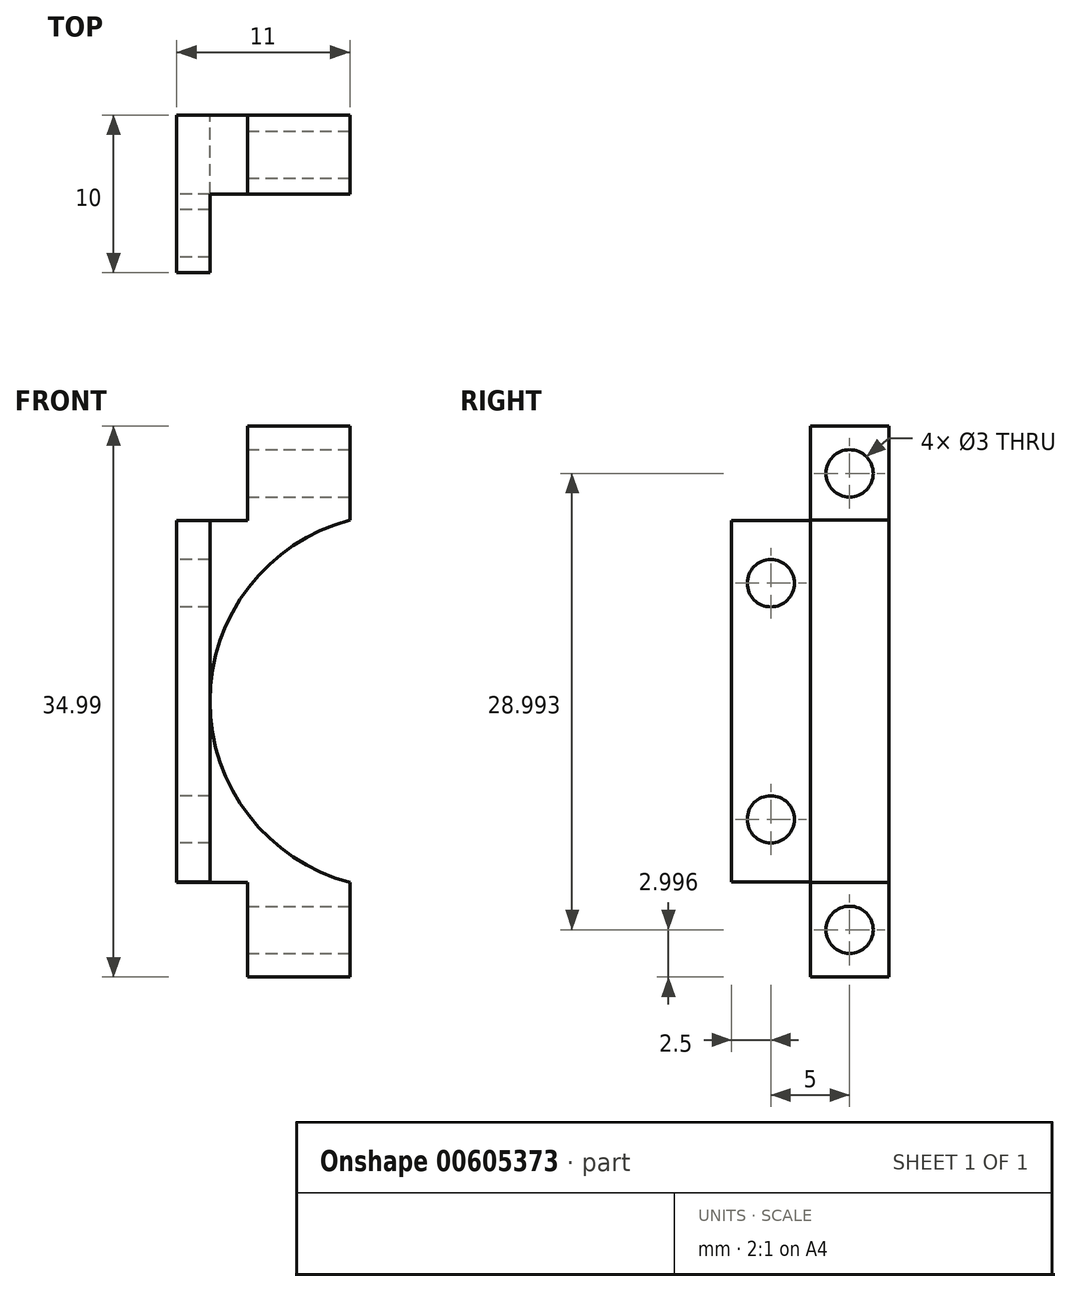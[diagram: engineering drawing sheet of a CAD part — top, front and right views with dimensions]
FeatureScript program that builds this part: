
annotation { "Feature Type Name" : "Feature", "Feature Type Description" : "" }
export const myFeature = defineFeature(function(context is Context, id is Id, definition is map)
    precondition{}
    {
        {
            var Q0;
            Q0=qCreatedBy(makeId("Front.planeOp"),FACE);
            var sketch = newSketch(context, id + "F0", { "sketchPlane" : qUnion([Q0])});
            skArc(sketch, "E0", {"start": v(0, 11.5) * mm, "mid": v(-8.88, 0) * mm, "end": v(0, -11.5) * mm});
            skLineSegment(sketch, "E1", {"start": v(0, -11.5) * mm, "end": v(0, -17.51) * mm});
            skLineSegment(sketch, "E2", {"start": v(0, -17.51) * mm, "end": v(-2, -17.51) * mm});
            skLineSegment(sketch, "E3", {"start": v(-2, -17.51) * mm, "end": v(-2, -11.51) * mm});
            skLineSegment(sketch, "E4", {"start": v(-2, -11.51) * mm, "end": v(-11, -11.51) * mm});
            skLineSegment(sketch, "E5", {"start": v(-11, -11.51) * mm, "end": v(-11, 11.48) * mm});
            skLineSegment(sketch, "E6", {"start": v(-11, 11.48) * mm, "end": v(-2, 11.48) * mm});
            skLineSegment(sketch, "E7", {"start": v(-2, 11.48) * mm, "end": v(-2, 17.48) * mm});
            skLineSegment(sketch, "E8", {"start": v(-2, 17.48) * mm, "end": v(0, 17.48) * mm});
            skLineSegment(sketch, "E9", {"start": v(0, 17.48) * mm, "end": v(0, 11.5) * mm});
            skLineSegment(sketch, "E10.bottom", {"start": v(-2, 17.48) * mm, "end": v(-6.5, 17.48) * mm});
            skLineSegment(sketch, "E10.top", {"start": v(-2, 11.48) * mm, "end": v(-6.5, 11.48) * mm});
            skLineSegment(sketch, "E10.left", {"start": v(-2, 17.48) * mm, "end": v(-2, 11.48) * mm});
            skLineSegment(sketch, "E10.right", {"start": v(-6.5, 17.48) * mm, "end": v(-6.5, 11.48) * mm});
            skLineSegment(sketch, "E11.bottom", {"start": v(-6.5, -11.51) * mm, "end": v(-2, -11.51) * mm});
            skLineSegment(sketch, "E11.top", {"start": v(-6.5, -17.51) * mm, "end": v(-2, -17.51) * mm});
            skLineSegment(sketch, "E11.left", {"start": v(-6.5, -11.51) * mm, "end": v(-6.5, -17.51) * mm});
            skLineSegment(sketch, "E11.right", {"start": v(-2, -11.51) * mm, "end": v(-2, -17.51) * mm});
            skSolve(sketch);
        }
        {
            var Q0;
            Q0=qSketchRegion(id+"F0",true);
            extrude(context, id + "F1", {"entities" : qUnion([Q0]), "depth" : 5 * mm, "offsetDistance" : 25 * mm});
        }
        {
            var Q0;
            Q0=makeQuery(id+"F1.opExtrude","SWEPT_FACE",FACE,{"disambiguationData":[OSD([sQuery(id+"F0.wireOp",EDGE,"E9")])]});
            var sketch = newSketch(context, id + "F2", { "sketchPlane" : qUnion([Q0])});
            skCircle(sketch, "E12", {"center": v(-2.5, 14.48) * mm, "radius": 1.5 * mm});
            skPoint(sketch, "E12.centerSnap0", {"position": v(0, 14.48) * mm});
            skPoint(sketch, "E12.centerSnap1", {"position": v(-2.5, 11.5) * mm});
            skCircle(sketch, "E13", {"center": v(-2.5, -14.51) * mm, "radius": 1.5 * mm});
            skSolve(sketch);
        }
        {
            var Q0;
            Q0=qSketchRegion(id+"F2",true);
            extrude(context, id + "F3", {"entities" : qUnion([Q0]), "operationType" : NewBodyOperationType.REMOVE, "oppositeDirection" : true, "depth" : 25 * mm, "offsetDistance" : 25 * mm});
        }
        {
            var Q0;
            Q0=makeQuery(id+"F1.opExtrude","CAP_FACE",FACE,{"disambiguationData":[OSD([sQuery(id+"F0.wireOp",EDGE,"E0"),sQuery(id+"F0.wireOp",EDGE,"E1"),sQuery(id+"F0.wireOp",EDGE,"E2"),sQuery(id+"F0.wireOp",EDGE,"E4"),sQuery(id+"F0.wireOp",EDGE,"E5"),sQuery(id+"F0.wireOp",EDGE,"E6"),sQuery(id+"F0.wireOp",EDGE,"E8"),sQuery(id+"F0.wireOp",EDGE,"E9"),sQuery(id+"F0.wireOp",EDGE,"E10.bottom"),sQuery(id+"F0.wireOp",EDGE,"E10.right"),sQuery(id+"F0.wireOp",EDGE,"E11.top"),sQuery(id+"F0.wireOp",EDGE,"E11.left")])],"isStart":false});
            var sketch = newSketch(context, id + "F4", { "sketchPlane" : qUnion([Q0])});
            skLineSegment(sketch, "E14.bottom", {"start": v(-8.88, 11.48) * mm, "end": v(-11, 11.48) * mm});
            skLineSegment(sketch, "E14.top", {"start": v(-8.88, -11.48) * mm, "end": v(-11, -11.48) * mm});
            skLineSegment(sketch, "E14.left", {"start": v(-8.88, 11.48) * mm, "end": v(-8.88, -11.48) * mm});
            skLineSegment(sketch, "E14.right", {"start": v(-11, 11.48) * mm, "end": v(-11, -11.48) * mm});
            skPoint(sketch, "E14.middle", {"position": v(-9.94, 0) * mm});
            skPoint(sketch, "E14.middle.positionSnap0", {"position": v(-8.88, 0) * mm});
            skPoint(sketch, "E14.cornerSnap0", {"position": v(-8.88, 0) * mm});
            skPoint(sketch, "E14.centerSnap0", {"position": v(-8.88, 0) * mm});
            skSolve(sketch);
        }
        {
            var Q0;
            Q0=qSketchRegion(id+"F4",true);
            extrude(context, id + "F5", {"entities" : qUnion([Q0]), "operationType" : NewBodyOperationType.ADD, "depth" : 5 * mm, "offsetDistance" : 25 * mm});
        }
        {
            var Q0;
            Q0=makeQuery(id+"F5.boolean.opBoolean","MERGE",FACE,{"derivedFrom":[makeQuery(id+"F1.opExtrude","SWEPT_FACE",FACE,{"disambiguationData":[OSD([sQuery(id+"F0.wireOp",EDGE,"E5")])]}),makeQuery(id+"F5.opExtrude","SWEPT_FACE",FACE,{"disambiguationData":[OSD([sQuery(id+"F4.wireOp",EDGE,"E14.right")])]})]});
            var sketch = newSketch(context, id + "F6", { "sketchPlane" : qUnion([Q0])});
            skCircle(sketch, "E15", {"center": v(7.5, 7.5) * mm, "radius": 1.5 * mm});
            skCircle(sketch, "E16", {"center": v(7.5, -7.5) * mm, "radius": 1.5 * mm});
            skSolve(sketch);
        }
        {
            var Q0;
            Q0=qSketchRegion(id+"F6",true);
            extrude(context, id + "F7", {"entities" : qUnion([Q0]), "operationType" : NewBodyOperationType.REMOVE, "oppositeDirection" : true, "depth" : 25 * mm, "offsetDistance" : 25 * mm});
        }
    });
